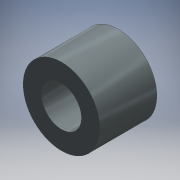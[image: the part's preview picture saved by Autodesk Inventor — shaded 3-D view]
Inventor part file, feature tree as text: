
AUTODESK INVENTOR PART (.ipt)
format: ipt  version: 2016 (Build 200138000, 138)  size: 107,520 bytes
history: native  units: mm
features: extrude x1, sketch x1
ambient origin geometry x8: Origin, YZ Plane, XZ Plane, XY Plane, X Axis, Y Axis, Z Axis, Center Point
bodies: Solid1 (feature_tree)
feature tree (2):
  extrude  "Extrusion1"  Depth=8.715mm
  sketch  "Sketch1"  dims[d0=6.1mm d1=11.75mm d2=8.715mm d3=0.0mm]
